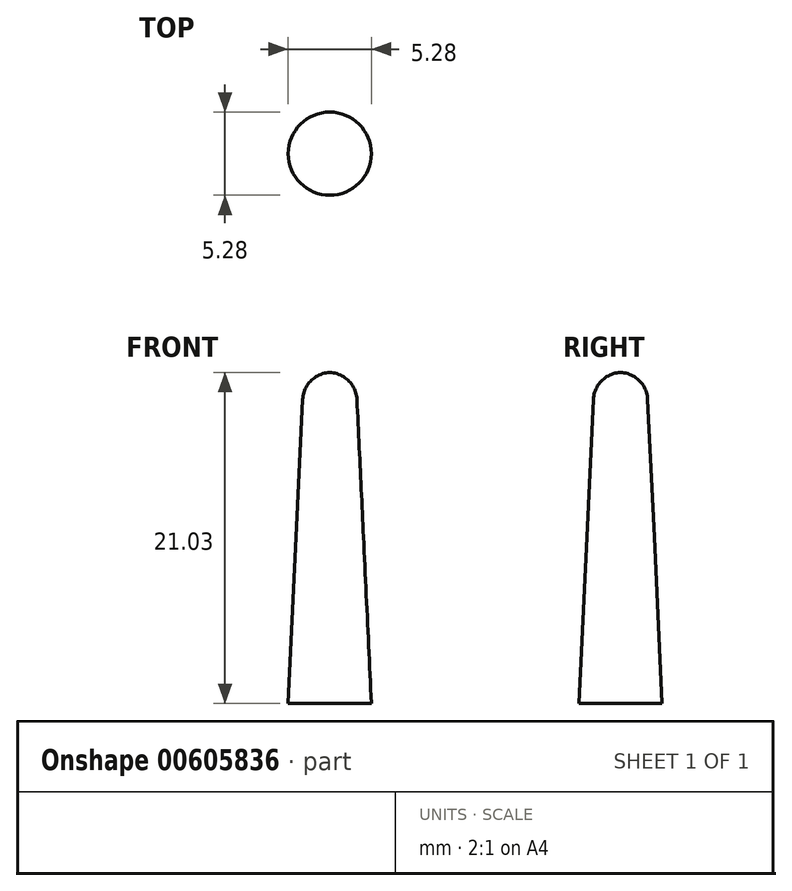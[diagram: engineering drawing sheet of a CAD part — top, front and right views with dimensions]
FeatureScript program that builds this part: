
annotation { "Feature Type Name" : "Feature", "Feature Type Description" : "" }
export const myFeature = defineFeature(function(context is Context, id is Id, definition is map)
    precondition{}
    {
        {
            var Q0;
            Q0=qCreatedBy(makeId("Front.planeOp"),FACE);
            var sketch = newSketch(context, id + "F0", { "sketchPlane" : qUnion([Q0])});
            skLineSegment(sketch, "E0", {"start": v(0.08, 21.8) * mm, "end": v(0.08, 11.36) * mm});
            skLineSegment(sketch, "E1", {"start": v(1.8, 20.08) * mm, "end": v(2.23, 11.36) * mm});
            skArc(sketch, "E2", {"start": v(1.8, 20.08) * mm, "mid": v(1.28, 21.28) * mm, "end": v(0.08, 21.8) * mm});
            skLineSegment(sketch, "E3", {"start": v(0.08, 11.36) * mm, "end": v(0.08, 0.78) * mm});
            skLineSegment(sketch, "E4", {"start": v(0.08, 0.78) * mm, "end": v(2.72, 0.78) * mm});
            skLineSegment(sketch, "E5", {"start": v(2.23, 11.36) * mm, "end": v(2.72, 0.78) * mm});
            skSolve(sketch);
        }
        {
            var Q0;
            Q0=makeQuery(id+"F0.imprint","IMPRINT",FACE,{"disambiguationData":[TD([[makeQuery(id+"F0.imprint","IMPRINT",EDGE,{"derivedFrom":sQuery(id+"F0.wireOp",EDGE,"E0")}),1.0]])]});
            var Q1;
            Q1=sQuery(id+"F0.wireOp",EDGE,"E3");
            revolve(context, id + "F1", {"entities" : qUnion([Q0]), "axis" : qUnion([Q1]), "revolveType" : RevolveType.FULL});
        }
    });
